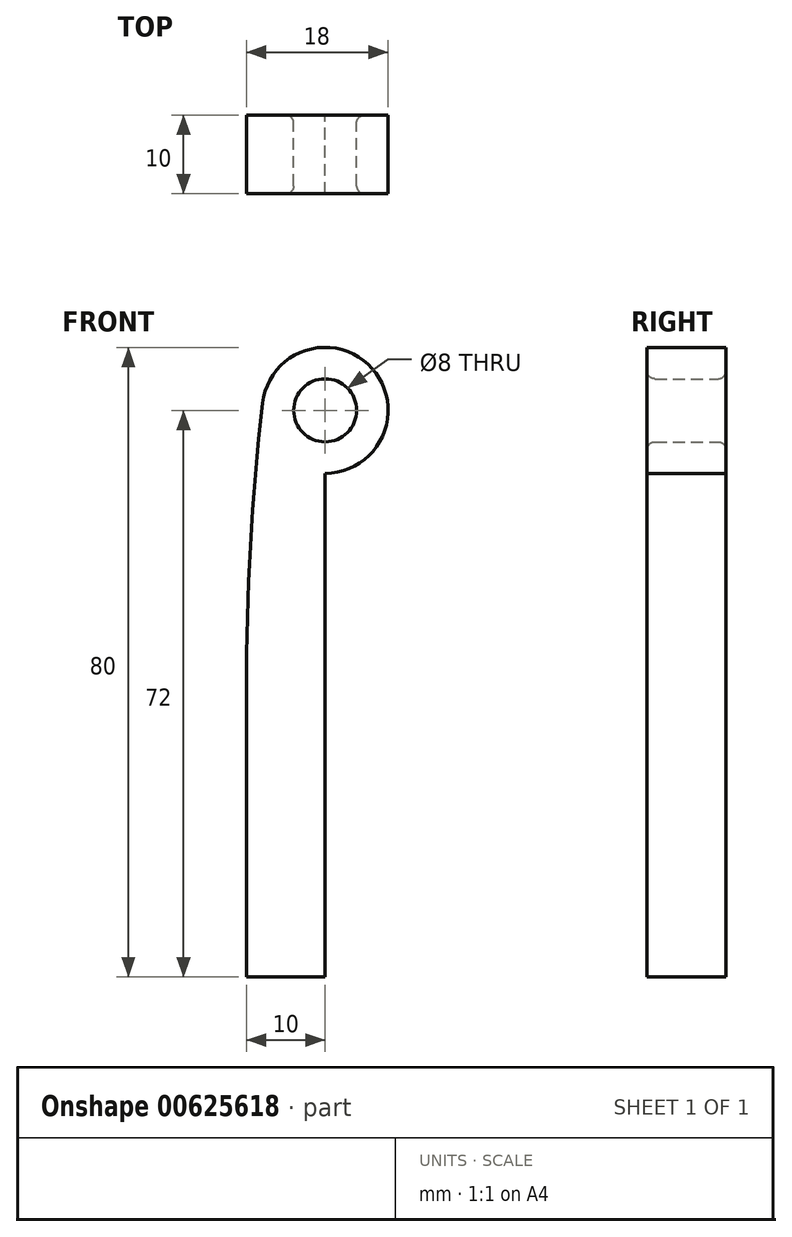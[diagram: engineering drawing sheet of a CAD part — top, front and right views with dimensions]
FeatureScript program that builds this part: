
annotation { "Feature Type Name" : "Feature", "Feature Type Description" : "" }
export const myFeature = defineFeature(function(context is Context, id is Id, definition is map)
    precondition{}
    {
        {
            var Q0;
            Q0=qCreatedBy(makeId("Front.planeOp"),FACE);
            var sketch = newSketch(context, id + "F0", { "sketchPlane" : qUnion([Q0])});
            skLineSegment(sketch, "E0.bottom", {"start": v(0, 0) * mm, "end": v(10, 0) * mm});
            skLineSegment(sketch, "E0.left", {"start": v(0, 0) * mm, "end": v(0, 36.58) * mm});
            skLineSegment(sketch, "E0.right", {"start": v(10, 0) * mm, "end": v(10, 64) * mm});
            skArc(sketch, "E1", {"start": v(10, 64) * mm, "mid": v(15.97, 77.33) * mm, "end": v(2.05, 72.9) * mm});
            skCircle(sketch, "E2", {"center": v(10, 72) * mm, "radius": 4 * mm});
            skArc(sketch, "E3", {"start": v(2.05, 72.9) * mm, "mid": v(0.51, 54.77) * mm, "end": v(0, 36.58) * mm});
            skSolve(sketch);
        }
        {
            var Q0;
            Q0=makeQuery(id+"F0.imprint","IMPRINT",FACE,{"disambiguationData":[TD([[makeQuery(id+"F0.imprint","IMPRINT",EDGE,{"derivedFrom":sQuery(id+"F0.wireOp",EDGE,"E0.bottom")}),1.0]])]});
            extrude(context, id + "F1", {"entities" : qUnion([Q0]), "endBound" : BoundingType.SYMMETRIC, "depth" : 10 * mm, "offsetDistance" : 25 * mm});
        }
        {
            var Q0;
            Q0=makeQuery(id+"F1.opExtrude","CAP_EDGE",EDGE,{"disambiguationData":[OSD([sQuery(id+"F0.wireOp",EDGE,"E2")])],"isStart":false});
            var Q1;
            Q1=makeQuery(id+"F1.opExtrude","CAP_EDGE",EDGE,{"disambiguationData":[OSD([sQuery(id+"F0.wireOp",EDGE,"E2")])],"isStart":true});
            fillet(context, id + "F2", {"entities" : qUnion([Q0, Q1]), "radius" : 1 * mm, "tangentPropagation" : true, "allowEdgeOverflow" : false});
        }
    });
